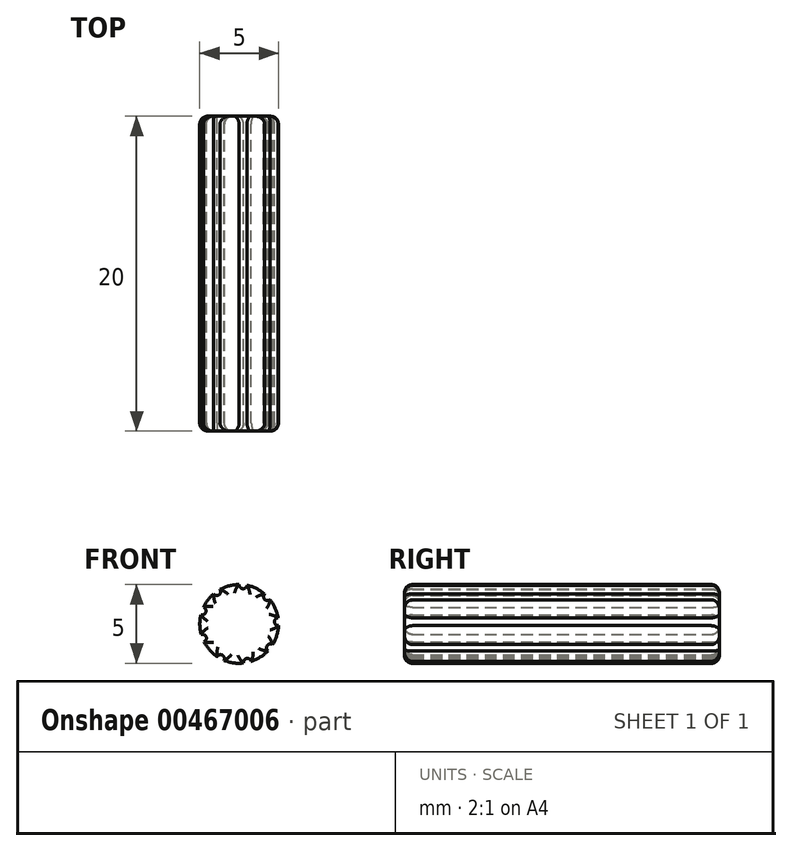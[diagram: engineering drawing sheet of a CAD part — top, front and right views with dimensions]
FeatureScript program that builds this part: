
annotation { "Feature Type Name" : "Feature", "Feature Type Description" : "" }
export const myFeature = defineFeature(function(context is Context, id is Id, definition is map)
    precondition{}
    {
        {
            var Q0;
            Q0=qCreatedBy(makeId("Front.planeOp"),FACE);
            var sketch = newSketch(context, id + "F0", { "sketchPlane" : qUnion([Q0])});
            skCircle(sketch, "E0", {"center": v(0, 0) * mm, "radius": 2.5 * mm});
            skCircle(sketch, "E1", {"center": v(-2.36, 0.83) * mm, "radius": 0.25 * mm});
            skCircle(sketch, "E2.1.0", {"center": v(-2.33, -0.9) * mm, "radius": 0.25 * mm});
            skCircle(sketch, "E2.2.0", {"center": v(-1.18, -2.2) * mm, "radius": 0.25 * mm});
            skCircle(sketch, "E2.3.0", {"center": v(0.53, -2.44) * mm, "radius": 0.25 * mm});
            skCircle(sketch, "E2.4.0", {"center": v(1.99, -1.51) * mm, "radius": 0.25 * mm});
            skCircle(sketch, "E2.5.0", {"center": v(2.5, 0.14) * mm, "radius": 0.25 * mm});
            skCircle(sketch, "E2.6.0", {"center": v(1.8, 1.73) * mm, "radius": 0.25 * mm});
            skCircle(sketch, "E2.7.0", {"center": v(0.25, 2.49) * mm, "radius": 0.25 * mm});
            skCircle(sketch, "E2.8.0", {"center": v(-1.42, 2.05) * mm, "radius": 0.25 * mm});
            skLineSegment(sketch, "E2.anchor1", {"start": v(0, 0) * mm, "end": v(-2.36, 0.83) * mm, "construction": true});
            skLineSegment(sketch, "E2.anchor2", {"start": v(0, 0) * mm, "end": v(-1.42, 2.05) * mm, "construction": true});
            skSolve(sketch);
        }
        {
            var Q0;
            {var subQ1=sQuery(id+"F0.wireOp",EDGE,"E0");var subQ24=sQuery(id+"F0.wireOp",EDGE,"E2.6.0");var subQ25=makeQuery(id+"F0.imprint","INTERSECT",VERTEX,{"disambiguationData":[OD(0.0)],"derivedFrom":[subQ1,subQ24]});Q0=makeQuery(id+"F0.imprint","IMPRINT",FACE,{"disambiguationData":[TD([[makeQuery(id+"F0.imprint","IMPRINT",EDGE,{"disambiguationData":[TD([[subQ25,1.0]])],"derivedFrom":subQ1}),1.0]])]});}
            extrude(context, id + "F1", {"entities" : qUnion([Q0]), "depth" : 20 * mm});
        }
        {
            var Q0;
            Q0=makeQuery(id+"F1.opExtrude","CAP_FACE",FACE,{"disambiguationData":[OSD([sQuery(id+"F0.wireOp",EDGE,"E0"),sQuery(id+"F0.wireOp",EDGE,"E1"),sQuery(id+"F0.wireOp",EDGE,"E2.1.0"),sQuery(id+"F0.wireOp",EDGE,"E2.2.0"),sQuery(id+"F0.wireOp",EDGE,"E2.3.0"),sQuery(id+"F0.wireOp",EDGE,"E2.4.0"),sQuery(id+"F0.wireOp",EDGE,"E2.5.0"),sQuery(id+"F0.wireOp",EDGE,"E2.6.0"),sQuery(id+"F0.wireOp",EDGE,"E2.7.0"),sQuery(id+"F0.wireOp",EDGE,"E2.8.0")])],"isStart":false});
            fillet(context, id + "F2", {"entities" : qUnion([Q0]), "radius" : 0.5 * mm, "tangentPropagation" : true, "allowEdgeOverflow" : false});
        }
        {
            var Q0;
            Q0=makeQuery(id+"F1.opExtrude","CAP_FACE",FACE,{"disambiguationData":[OSD([sQuery(id+"F0.wireOp",EDGE,"E0"),sQuery(id+"F0.wireOp",EDGE,"E1"),sQuery(id+"F0.wireOp",EDGE,"E2.1.0"),sQuery(id+"F0.wireOp",EDGE,"E2.2.0"),sQuery(id+"F0.wireOp",EDGE,"E2.3.0"),sQuery(id+"F0.wireOp",EDGE,"E2.4.0"),sQuery(id+"F0.wireOp",EDGE,"E2.5.0"),sQuery(id+"F0.wireOp",EDGE,"E2.6.0"),sQuery(id+"F0.wireOp",EDGE,"E2.7.0"),sQuery(id+"F0.wireOp",EDGE,"E2.8.0")])],"isStart":true});
            fillet(context, id + "F3", {"entities" : qUnion([Q0]), "radius" : 0.5 * mm, "tangentPropagation" : true, "allowEdgeOverflow" : false});
        }
    });
